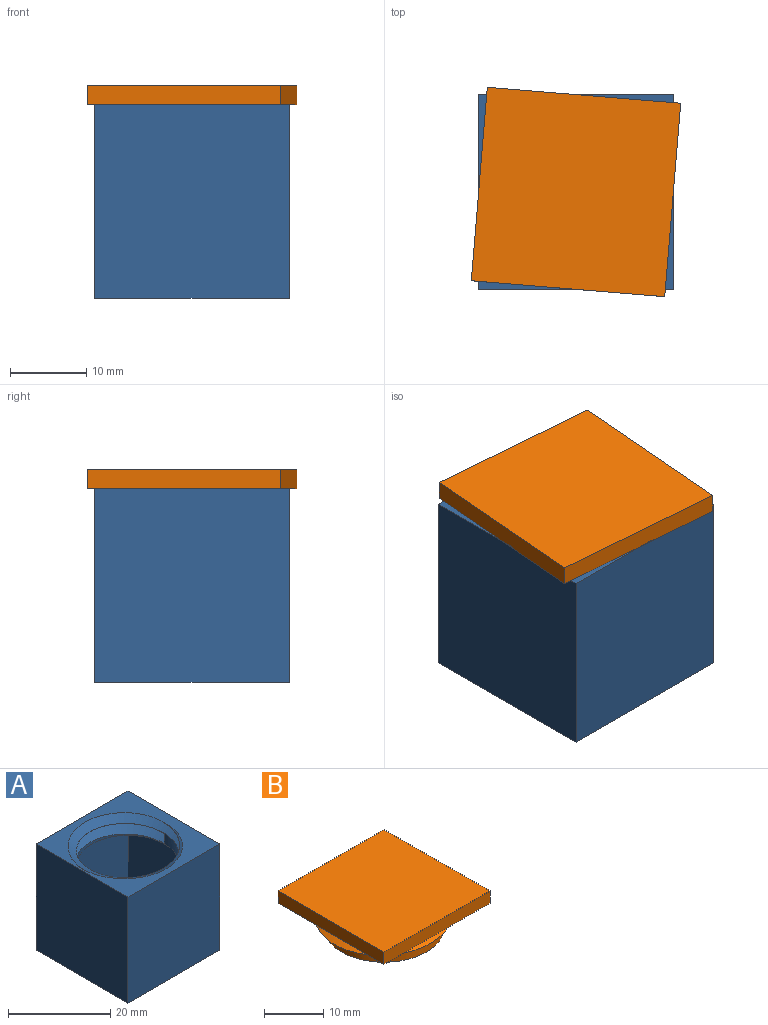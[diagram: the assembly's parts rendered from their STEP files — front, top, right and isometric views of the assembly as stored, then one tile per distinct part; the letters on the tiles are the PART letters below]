
ASSEMBLY  parts=2 mates=1
PART A: 17 faces, bbox 25.4x28.4x27.1 mm
  f0: plane 25.4x25.4mm, normal (0,0,1), area 251.2mm2, adj f2,f3,f4,f5,f6,f13,f14,f16
  f1: plane 25.4x25.4mm, normal (0,0,-1), area 645.2mm2, adj f2,f3,f4,f5
  f2: plane 25.4x25.4mm, normal (1,0,0), area 645.2mm2, adj f0,f1,f4,f5
  f3: plane 25.4x25.4mm, normal (-1,0,0), area 645.2mm2, adj f0,f1,f4,f5
  f4: plane 25.4x25.4mm, normal (0,-1,0), area 645.2mm2, adj f0,f1,f2,f3
  f5: plane 25.4x25.4mm, normal (0,1,0), area 645.2mm2, adj f0,f1,f2,f3
  f6: cylinder r=10.1mm len=20.2mm, axis (0,0,1), area 82mm2, adj f0,f7,f14,f15,f16
  f7: plane 20.32x20.32mm, normal (0,0,-1), area 92.5mm2, adj f6,f9,f10,f11,f12,f16
  f8: plane 20.32x20.32mm, normal (0,0,1), area 412.9mm2, adj f9,f10,f11,f12
  f9: plane 20.32x17.78mm, normal (0,-1,0), area 361.3mm2, adj f7,f8,f11,f12
  f10: plane 20.32x17.78mm, normal (0,1,0), area 361.3mm2, adj f7,f8,f11,f12
  f11: plane 20.32x17.78mm, normal (1,0,0), area 361.3mm2, adj f7,f8,f9,f10
  f12: plane 20.32x17.78mm, normal (-1,0,0), area 361.3mm2, adj f7,f8,f9,f10
  f13: plane 0x0mm, normal (0,-1,0), area 0mm2, adj f0,f16
  f14: bspline ~28.36x24.57mm, area 224mm2, adj f0,f6,f15,f16
  f15: plane 2.52x2.18mm, normal (0,1,0), area 2.7mm2, adj f6,f14,f16
  f16: bspline ~24.55x24.54mm, area 309mm2, adj f0,f6,f7,f13,f14,f15
PART B: 13 faces, bbox 26.2x27.5x8.4 mm
  f0: plane 26.16x26.16mm, normal (0,0,-1), area 290.8mm2, adj f2,f3,f4,f5,f6,f7,f10,f11
  f1: cylinder r=10.16mm len=20.32mm, axis (0,0,1), area 83.5mm2, adj f2,f9,f11,f12
  f2: cylinder r=10.16mm len=20.32mm, axis (0,0,1), area 58.4mm2, adj f0,f1,f3,f10,f11
  f3: cylinder r=10.16mm len=15.92mm, axis (0,0,1), area 9.7mm2, adj f0,f2,f10
  f4: plane 25.4x2.54mm, normal (0,-1,0), area 64.5mm2, adj f0,f5,f7,f8
  f5: plane 25.4x2.54mm, normal (1,0,0), area 64.5mm2, adj f0,f4,f6,f8
  f6: plane 25.4x2.54mm, normal (0,1,0), area 64.5mm2, adj f0,f5,f7,f8
  f7: plane 25.4x2.54mm, normal (-1,0,0), area 64.5mm2, adj f0,f4,f6,f8
  f8: plane 25.4x25.4mm, normal (0,0,1), area 645.2mm2, adj f4,f5,f6,f7
  f9: plane 20.32x20.32mm, normal (0,0,-1), area 324.3mm2, adj f1
  f10: bspline ~26.72x23.14mm, area 167.5mm2, adj f0,f2,f3,f11,f12
  f11: bspline ~26.72x23.14mm, area 202.2mm2, adj f0,f1,f2,f10,f12
  f12: plane 1.63x1.41mm, normal (0,-1,0), area 1.1mm2, adj f1,f10,f11
PLACE A t=(0,12.7,12.7)mm
PLACE B rot(axis=(0,0,-1),4.7deg) t=(0,0,25.32)mm
MATE cylindrical A.f6 <-> B.f1  axis (0,0,-1) through (0,0,20.32)mm
